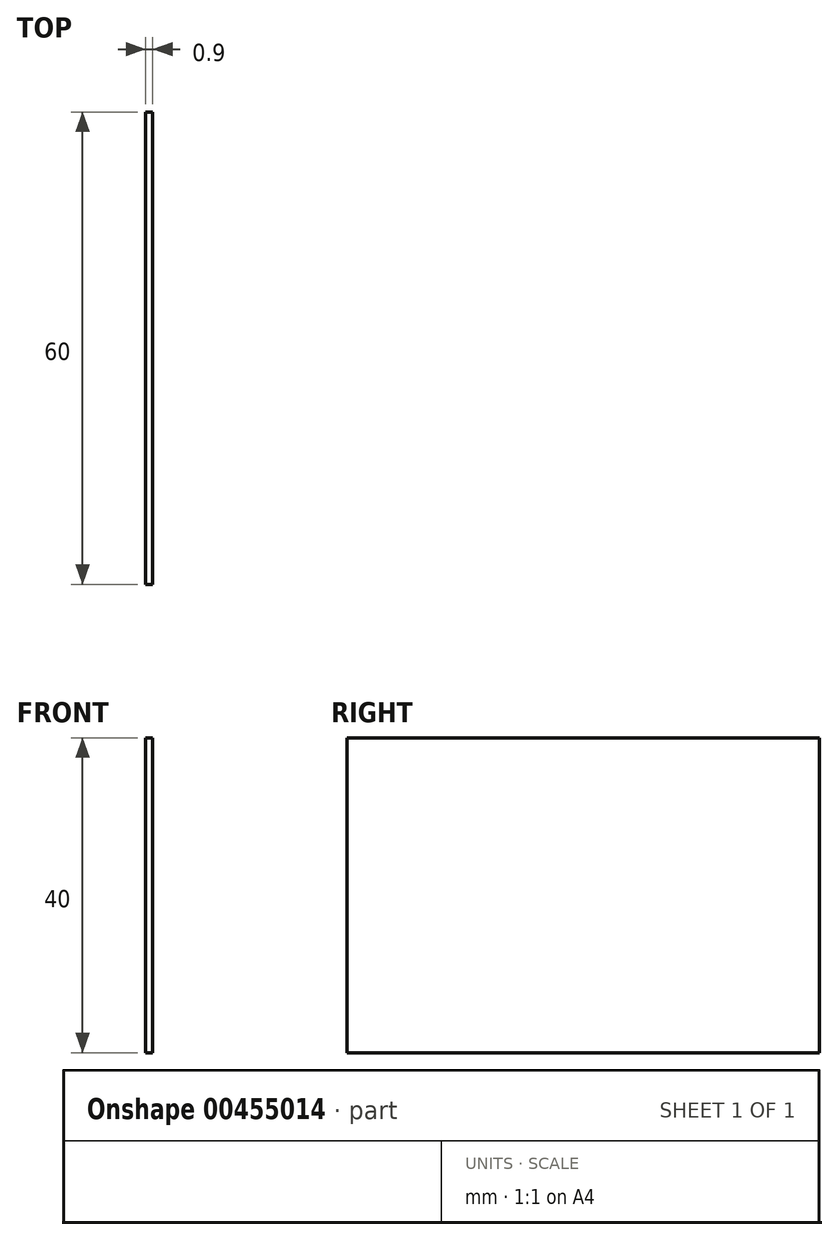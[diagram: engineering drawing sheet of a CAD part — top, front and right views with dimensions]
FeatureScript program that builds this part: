
annotation { "Feature Type Name" : "Feature", "Feature Type Description" : "" }
export const myFeature = defineFeature(function(context is Context, id is Id, definition is map)
    precondition{}
    {
        {
            var Q0;
            Q0=qCreatedBy(makeId("Front.planeOp"),FACE);
            var sketch = newSketch(context, id + "F0", { "sketchPlane" : qUnion([Q0])});
            skLineSegment(sketch, "E0.bottom", {"start": v(0, 0) * mm, "end": v(-0.9, 0) * mm});
            skLineSegment(sketch, "E0.top", {"start": v(0, 40) * mm, "end": v(-0.9, 40) * mm});
            skLineSegment(sketch, "E0.left", {"start": v(0, 0) * mm, "end": v(0, 40) * mm});
            skLineSegment(sketch, "E0.right", {"start": v(-0.9, 0) * mm, "end": v(-0.9, 40) * mm});
            skSolve(sketch);
        }
        {
            var Q0;
            Q0 = qSketchRegion(id + "F0", true);
            extrude(context, id + "F1", {"entities" : qUnion([Q0]), "depth" : 60 * mm});
        }
    });
